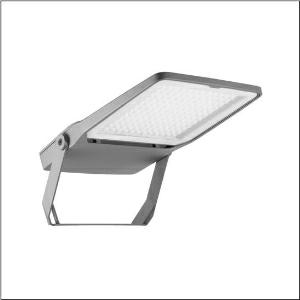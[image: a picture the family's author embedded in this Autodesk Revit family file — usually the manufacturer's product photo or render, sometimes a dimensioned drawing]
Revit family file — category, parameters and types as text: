
# Revit family: floodlight_fl_20_midi___pl61_5xa7682e3c1ac_6cc9
name_source: partatom
category: Lighting Fixtures
units: mm (PartAtom-declared; Revit-internal decimal feet)

## family parameters
Cut with Voids When Loaded = No
Host = Face
Light Source = No
Part Type = Normal
Room Calculation Point = No
Round Connector Dimension = Use Diameter
Shared = No

## types (1)
- --- (1 x LED 5000K / CRI = 70 (unbekannt), 27570 lm, 5000K)
    Apparent Load = 208 VA
    CIE Flux Codes = 33 65 98 100 100
    Color Rendering = 70
    Color Temperature = 5000K
    Default Elevation = 1800 mm
    Description = Floodlight FL 20 midi, floodlight, primary light control with lens, of plastic, primary optical cover: protective disc, of toughened safety glass, transparent, light distribution: PL61, light emission: direct distribution, primary light characteristic: asymmetric, installation type: surface-mounted, LED, High Power LED, rated luminous flux: 27.570lm, luminous efficacy: 133lm/W, light colour: 750, colour temperature: 5000K, control gear: ECG Plus, control: flexible luminous flux parameterisation, time-dependent luminous flux control, digital communication interface, power reduction, overheat protection, electronic power reduction, with terminal, 5-pole, max. 2.5mm², mains connection: 220..240V, AC, 50/60Hz, rated input power: 208W, LED unit, of diecast aluminium, powder-coated, Siteco® metallic grey (DB 702S), corrosivity category C5 mid according to DIN EN ISO 12944, incl. 1x M20 cable gland for cable Ø 6.5..12mm, length: 654mm, width: 450mm, height: 76mm, housing frame, of diecast aluminium, powder-coated, Siteco® metallic grey (DB 702S), mounting bracket, of steel, powder-coated, Siteco® metallic grey (DB 702S), DALI, protection rating (complete): IP66, insulation class (complete): insulation class II (safety insulation), certification: CE, ENEC, VDE, protection symbol: D, permissible operating ambient temperature: -40..+40°C, permissible operating ambient temperature for outdoor applications: -40..+50°C, standard: DIN EN 12944, packaging unit: 1 piece

Light Distribution: PL61
    Height = 76 mm
    Lamp = 1 x LED 5000K / CRI >= 70 (unbekannt)
    Lamp Light Flux = 27570 lm
    Lamp count = 1
    Length = 672 mm
    Luminous efficacy = 133 lm/W
    Manufacturer = Siteco
    ModVariant = No
    Model = 5XA7682E3C1AC
    Mounting Place = Wall
    Mounting Type = Surface mounted
    Number of Poles = 1
    OnlyDefault = Yes
    Power Factor = 1
    Product Name = Floodlight FL 20 midi | PL61
    Product group = floodlight | wall mounted
    ProductGroupID = 2001
    Protection Class = Protection class II
    Protection Degree = IP 66
    RLX_Detail_Level = 1
    RLX_Emergency_Light_Flux = 0 lm
    RLX_Emergency_Type = 0
    RLX_Emergency_Type_DB = No
    RlxData = <blob elided: 98149 chars, md5=bb9bbd8c>
    Socket = socket
    Standby Power = 0 W
    System Light Flux = 27570 lm
    System Power = 208 W
    Type Comments = factory setting: luminous flux: 100 % | dim-lin: 254 | 484 mA
    Type Image = l_1005943.jpg
    URL = http://relux.com
    VarID = @adj_146845
    Voltage = 0 V
    Weight = 0.00 kg
    Width = 450 mm

## geometry (parser evidence)
native form markers: Blend x4, Sweep x12
no freeform markers — native parametric forms only
